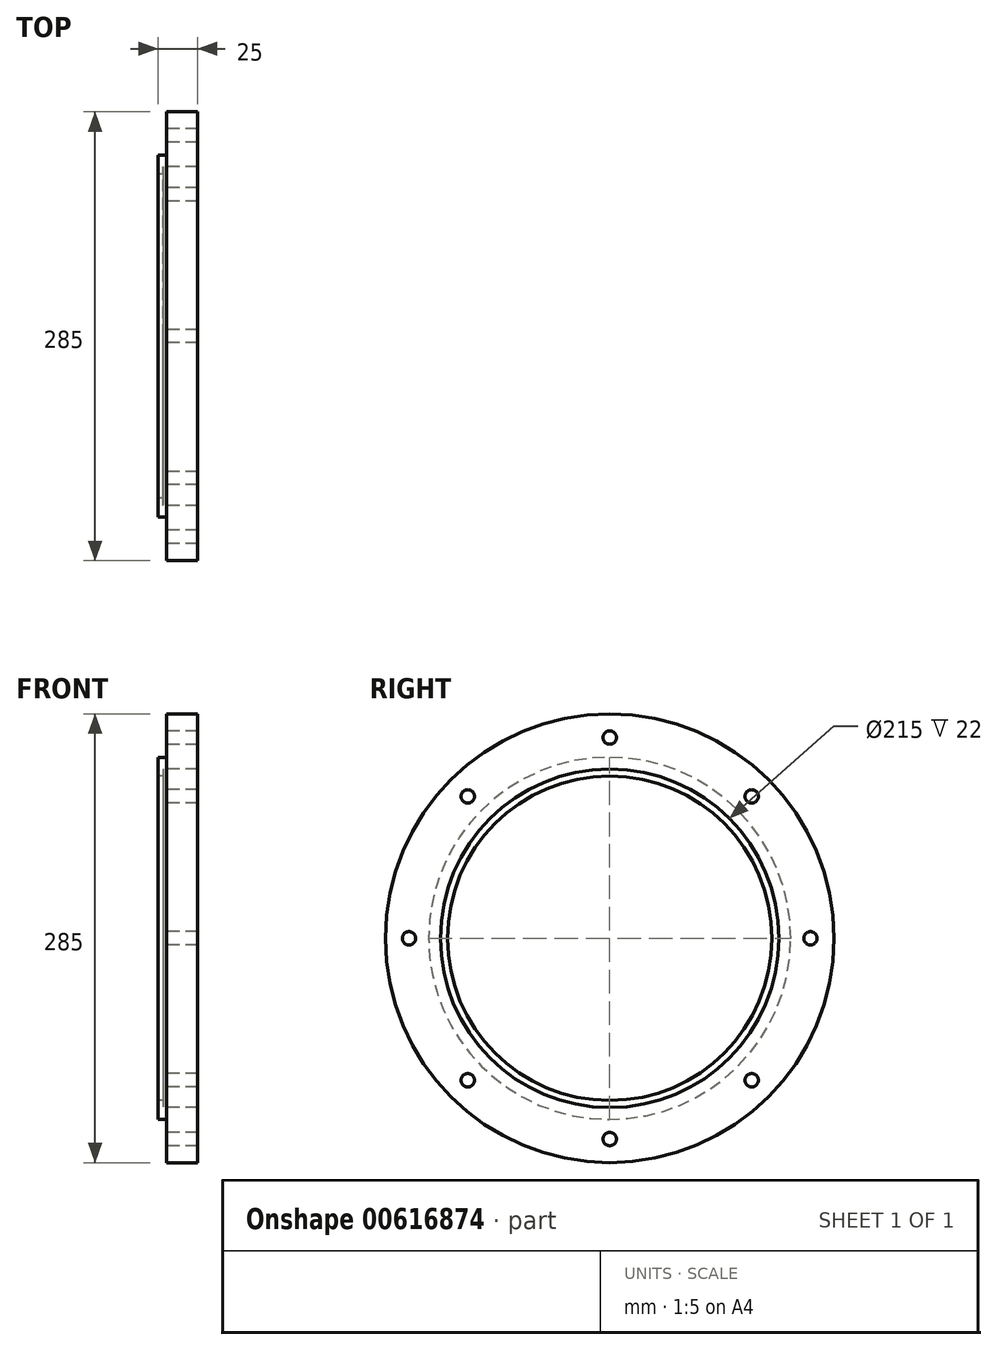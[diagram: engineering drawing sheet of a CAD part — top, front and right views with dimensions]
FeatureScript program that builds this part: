
annotation { "Feature Type Name" : "Feature", "Feature Type Description" : "" }
export const myFeature = defineFeature(function(context is Context, id is Id, definition is map)
    precondition{}
    {
        {
            var Q0;
            Q0=qCreatedBy(makeId("Front.planeOp"),FACE);
            var sketch = newSketch(context, id + "F0", { "sketchPlane" : qUnion([Q0])});
            skLineSegment(sketch, "E0", {"start": v(0, 115) * mm, "end": v(5.5, 115) * mm});
            skLineSegment(sketch, "E1", {"start": v(5.5, 115) * mm, "end": v(5.5, 142.5) * mm});
            skLineSegment(sketch, "E2", {"start": v(5.5, 142.5) * mm, "end": v(25, 142.5) * mm});
            skLineSegment(sketch, "E3", {"start": v(25, 142.5) * mm, "end": v(25, 107.5) * mm});
            skLineSegment(sketch, "E4", {"start": v(25, 107.5) * mm, "end": v(3, 107.5) * mm});
            skLineSegment(sketch, "E5", {"start": v(0, 107.5) * mm, "end": v(0, 115) * mm});
            skLineSegment(sketch, "E6", {"start": v(0, 0) * mm, "end": v(240.41, 0) * mm, "construction": true});
            skLineSegment(sketch, "E7", {"start": v(3, 107.5) * mm, "end": v(3, 103) * mm});
            skLineSegment(sketch, "E8", {"start": v(3, 103) * mm, "end": v(0, 103) * mm});
            skLineSegment(sketch, "E9", {"start": v(0, 103) * mm, "end": v(0, 107.5) * mm});
            skSolve(sketch);
        }
        {
            var Q0;
            Q0 = qSketchRegion(id + "F0", true);
            var Q1;
            Q1 = qConstructionFilter(qBodyType(qCreatedBy(id + "F0" ,EDGE), BodyType.WIRE), ConstructionObject.NO);
            var Q2;
            Q2=sQuery(id+"F0.wireOp",EDGE,"E6");
            revolve(context, id + "F1", {"surfaceOperationType" : NewSurfaceOperationType.NEW, "entities" : qUnion([Q0]), "surfaceEntities" : qUnion([Q1]), "axis" : qUnion([Q2]), "revolveType" : RevolveType.FULL});
        }
        {
            var Q0;
            Q0=makeQuery(id+"F1.opRevolve","SWEPT_FACE",FACE,{"disambiguationData":[OSD([sQuery(id+"F0.wireOp",EDGE,"E3")])]});
            var sketch = newSketch(context, id + "F2", { "sketchPlane" : qUnion([Q0])});
            skCircle(sketch, "E10", {"center": v(0, 0) * mm, "radius": 127.5 * mm, "construction": true});
            skCircle(sketch, "E11", {"center": v(0, 127.5) * mm, "radius": 5 * mm});
            skCircle(sketch, "E12.0", {"center": v(0, 0) * mm, "radius": 115 * mm, "construction": true});
            skCircle(sketch, "E13.1.0", {"center": v(-90.16, 90.16) * mm, "radius": 5 * mm});
            skCircle(sketch, "E13.2.0", {"center": v(-127.5, 0) * mm, "radius": 5 * mm});
            skCircle(sketch, "E13.3.0", {"center": v(-90.16, -90.16) * mm, "radius": 5 * mm});
            skCircle(sketch, "E13.4.0", {"center": v(0, -127.5) * mm, "radius": 5 * mm});
            skCircle(sketch, "E13.5.0", {"center": v(90.16, -90.16) * mm, "radius": 5 * mm});
            skCircle(sketch, "E13.6.0", {"center": v(127.5, 0) * mm, "radius": 5 * mm});
            skCircle(sketch, "E13.7.0", {"center": v(90.16, 90.16) * mm, "radius": 5 * mm});
            skSolve(sketch);
        }
        {
            var Q0;
            Q0=sQuery(id+"F2.wireOp",VERTEX,"E11.center");
            var Q1;
            Q1=sQuery(id+"F2.wireOp",VERTEX,"E13.7.0.center");
            var Q2;
            Q2=sQuery(id+"F2.wireOp",VERTEX,"E13.6.0.center");
            var Q3;
            Q3=sQuery(id+"F2.wireOp",VERTEX,"E13.5.0.center");
            var Q4;
            Q4=sQuery(id+"F2.wireOp",VERTEX,"E13.4.0.center");
            var Q5;
            Q5=sQuery(id+"F2.wireOp",VERTEX,"E13.3.0.center");
            var Q6;
            Q6=sQuery(id+"F2.wireOp",VERTEX,"E13.2.0.center");
            var Q7;
            Q7=sQuery(id+"F2.wireOp",VERTEX,"E13.1.0.center");
            var Q8;
            Q8=makeQuery(id+"F1.opRevolve","SWEPT_BODY",BODY,{"disambiguationData":[OSD([sQuery(id+"F0.wireOp",EDGE,"E0"),sQuery(id+"F0.wireOp",EDGE,"E1"),sQuery(id+"F0.wireOp",EDGE,"E2"),sQuery(id+"F0.wireOp",EDGE,"E3"),sQuery(id+"F0.wireOp",EDGE,"E4"),sQuery(id+"F0.wireOp",EDGE,"HMcSShfi-BQUH-JYmb-m6WX-gnk7d0lBlowP"),sQuery(id+"F0.wireOp",EDGE,"896H348g-fNVY-6h2H-eopK-1GxBHDQiiEOX"),sQuery(id+"F0.wireOp",EDGE,"E5")])]});
            hole(context, id + "F3", {"style" : HoleStyle.SIMPLE, "endStyle" : HoleEndStyle.BLIND, "standardTappedOrClearance" : lookupTablePath({ "standard" : "ISO", "engagement" : "75%", "pitch" : "1.5 mm", "size" : "M10", "type" : "Tapped" }), "standardBlindInLast" : lookupTablePath({ "standard" : "ISO", "engagement" : "75%", "pitch" : "1.5 mm", "size" : "M10", "type" : "Tapped" }), "holeDiameter" : 8.5 * mm, "majorDiameter" : 10 * mm, "showTappedDepth" : true, "holeDepth" : 49.5 * mm, "isTappedThrough" : true, "tappedDepth" : 45 * mm, "tapClearance" : 3, "locations" : qUnion([Q0, Q1, Q2, Q3, Q4, Q5, Q6, Q7]), "scope" : qUnion([Q8]), "startStyle" : HoleStartStyle.PART});
        }
    });
